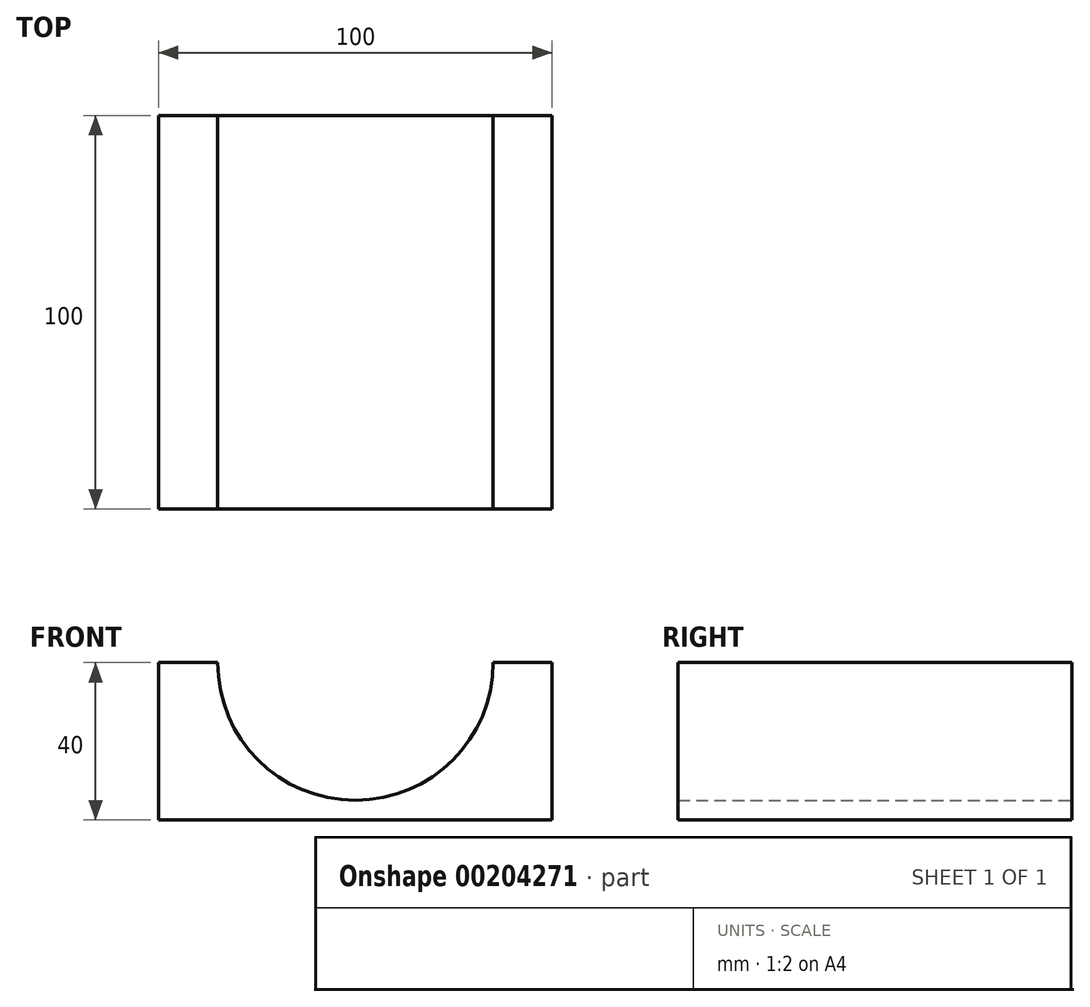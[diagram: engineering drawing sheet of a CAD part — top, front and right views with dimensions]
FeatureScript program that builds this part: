
annotation { "Feature Type Name" : "Feature", "Feature Type Description" : "" }
export const myFeature = defineFeature(function(context is Context, id is Id, definition is map)
    precondition{}
    {
        {
            var Q0;
            Q0=qCreatedBy(makeId("Front.planeOp"),FACE);
            var sketch = newSketch(context, id + "F0", { "sketchPlane" : qUnion([Q0])});
            skLineSegment(sketch, "E0.bottom", {"start": v(-50, 0) * mm, "end": v(0, 0) * mm});
            skLineSegment(sketch, "E0.top", {"start": v(-50, 40) * mm, "end": v(0, 40) * mm});
            skLineSegment(sketch, "E0.left", {"start": v(-50, 0) * mm, "end": v(-50, 40) * mm});
            skLineSegment(sketch, "E1.MirrorCS", {"start": v(50, 0) * mm, "end": v(0, 0) * mm});
            skLineSegment(sketch, "E2.MirrorCS", {"start": v(50, 0) * mm, "end": v(50, 40) * mm});
            skLineSegment(sketch, "E3.MirrorCS", {"start": v(50, 40) * mm, "end": v(0, 40) * mm});
            skArc(sketch, "E4", {"start": v(-35, 40) * mm, "mid": v(0, 5) * mm, "end": v(35, 40) * mm});
            skSolve(sketch);
        }
        {
            var Q0;
            Q0=makeQuery(id+"F0.imprint","IMPRINT",FACE,{"disambiguationData":[TD([[makeQuery(id+"F0.imprint","IMPRINT",EDGE,{"derivedFrom":sQuery(id+"F0.wireOp",EDGE,"E0.bottom")}),1.0]])]});
            extrude(context, id + "F1", {"entities" : qUnion([Q0]), "endBound" : BoundingType.SYMMETRIC, "depth" : 100 * mm});
        }
    });
